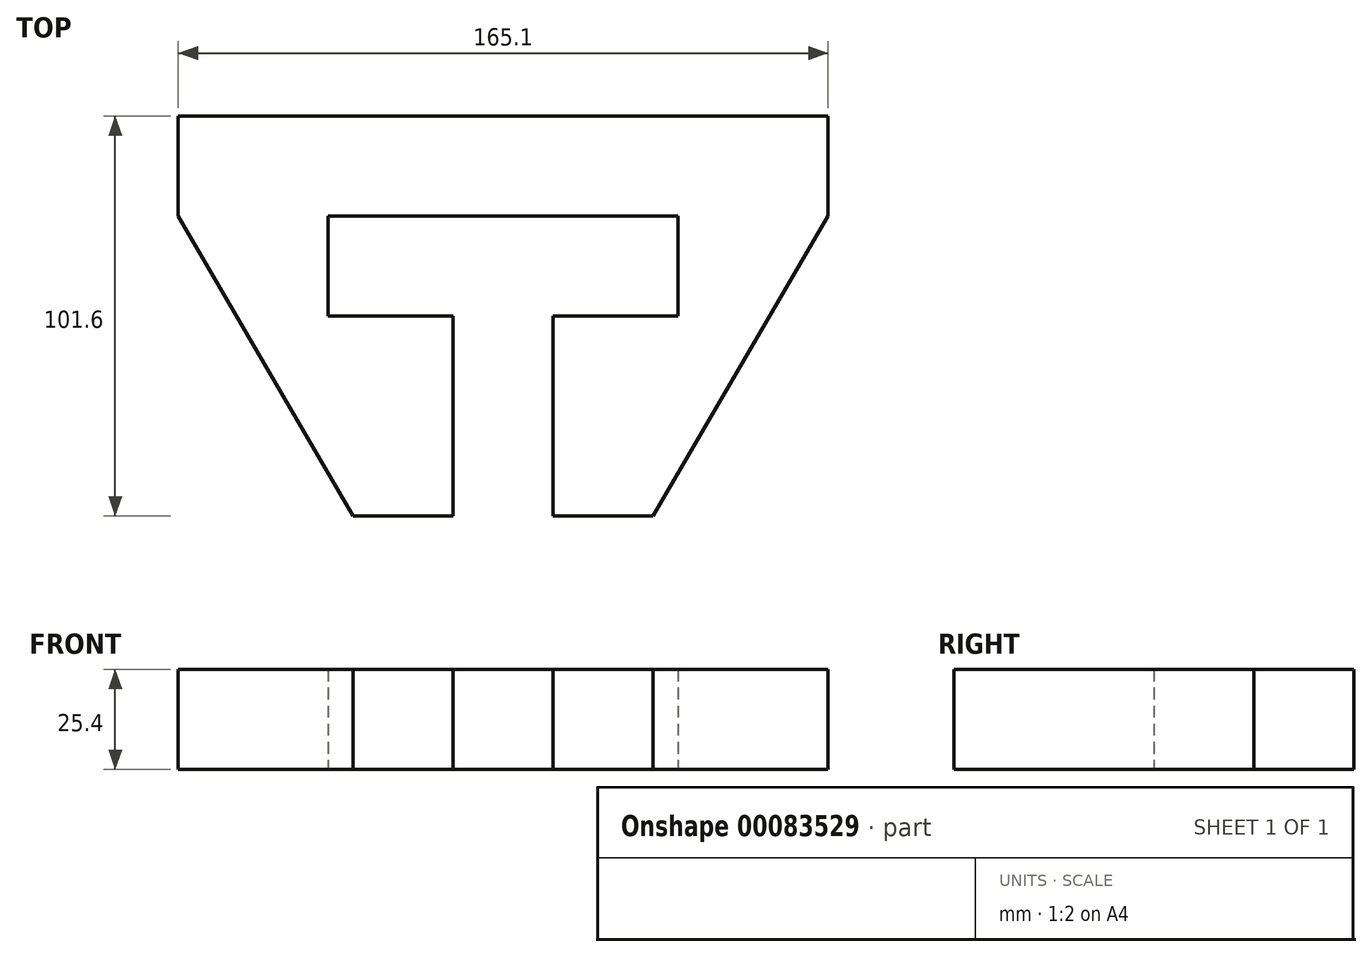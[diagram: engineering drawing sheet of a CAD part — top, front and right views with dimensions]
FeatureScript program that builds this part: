
annotation { "Feature Type Name" : "Feature", "Feature Type Description" : "" }
export const myFeature = defineFeature(function(context is Context, id is Id, definition is map)
    precondition{}
    {
        {
            var Q0;
            Q0=qCreatedBy(makeId("Top.planeOp"),FACE);
            var sketch = newSketch(context, id + "F0", { "sketchPlane" : qUnion([Q0])});
            skLineSegment(sketch, "E0", {"start": v(0, 50.8) * mm, "end": v(0, -50.8) * mm, "construction": true});
            skLineSegment(sketch, "E1", {"start": v(0, 50.8) * mm, "end": v(82.55, 50.8) * mm});
            skLineSegment(sketch, "E2", {"start": v(82.55, 50.8) * mm, "end": v(82.55, 25.4) * mm});
            skLineSegment(sketch, "E3", {"start": v(44.45, 25.4) * mm, "end": v(44.45, 0) * mm});
            skLineSegment(sketch, "E4", {"start": v(44.45, 0) * mm, "end": v(12.7, 0) * mm});
            skLineSegment(sketch, "E5", {"start": v(44.45, 25.4) * mm, "end": v(0, 25.4) * mm});
            skLineSegment(sketch, "E6", {"start": v(12.7, 0) * mm, "end": v(12.7, -50.8) * mm});
            skLineSegment(sketch, "E7", {"start": v(12.7, -50.8) * mm, "end": v(38.1, -50.8) * mm});
            skLineSegment(sketch, "E8", {"start": v(38.1, -50.8) * mm, "end": v(82.55, 25.4) * mm});
            skLineSegment(sketch, "E9", {"start": v(0, 25.4) * mm, "end": v(0, 50.8) * mm});
            skLineSegment(sketch, "E10.MirrorCS", {"start": v(-44.45, 0) * mm, "end": v(-12.7, 0) * mm});
            skLineSegment(sketch, "E11.MirrorCS", {"start": v(-44.45, 25.4) * mm, "end": v(0, 25.4) * mm});
            skLineSegment(sketch, "E12.MirrorCS", {"start": v(0, 50.8) * mm, "end": v(-82.55, 50.8) * mm});
            skLineSegment(sketch, "E13.MirrorCS", {"start": v(-12.7, 0) * mm, "end": v(-12.7, -50.8) * mm});
            skLineSegment(sketch, "E14.MirrorCS", {"start": v(-38.1, -50.8) * mm, "end": v(-82.55, 25.4) * mm});
            skLineSegment(sketch, "E15.MirrorCS", {"start": v(-12.7, -50.8) * mm, "end": v(-38.1, -50.8) * mm});
            skLineSegment(sketch, "E16.MirrorCS", {"start": v(-82.55, 50.8) * mm, "end": v(-82.55, 25.4) * mm});
            skLineSegment(sketch, "E17.MirrorCS", {"start": v(-44.45, 25.4) * mm, "end": v(-44.45, 0) * mm});
            skSolve(sketch);
        }
        {
            var Q0;
            Q0 = qSketchRegion(id + "F0", true);
            extrude(context, id + "F1", {"entities" : qUnion([Q0]), "depth" : 25.4 * mm});
        }
    });
